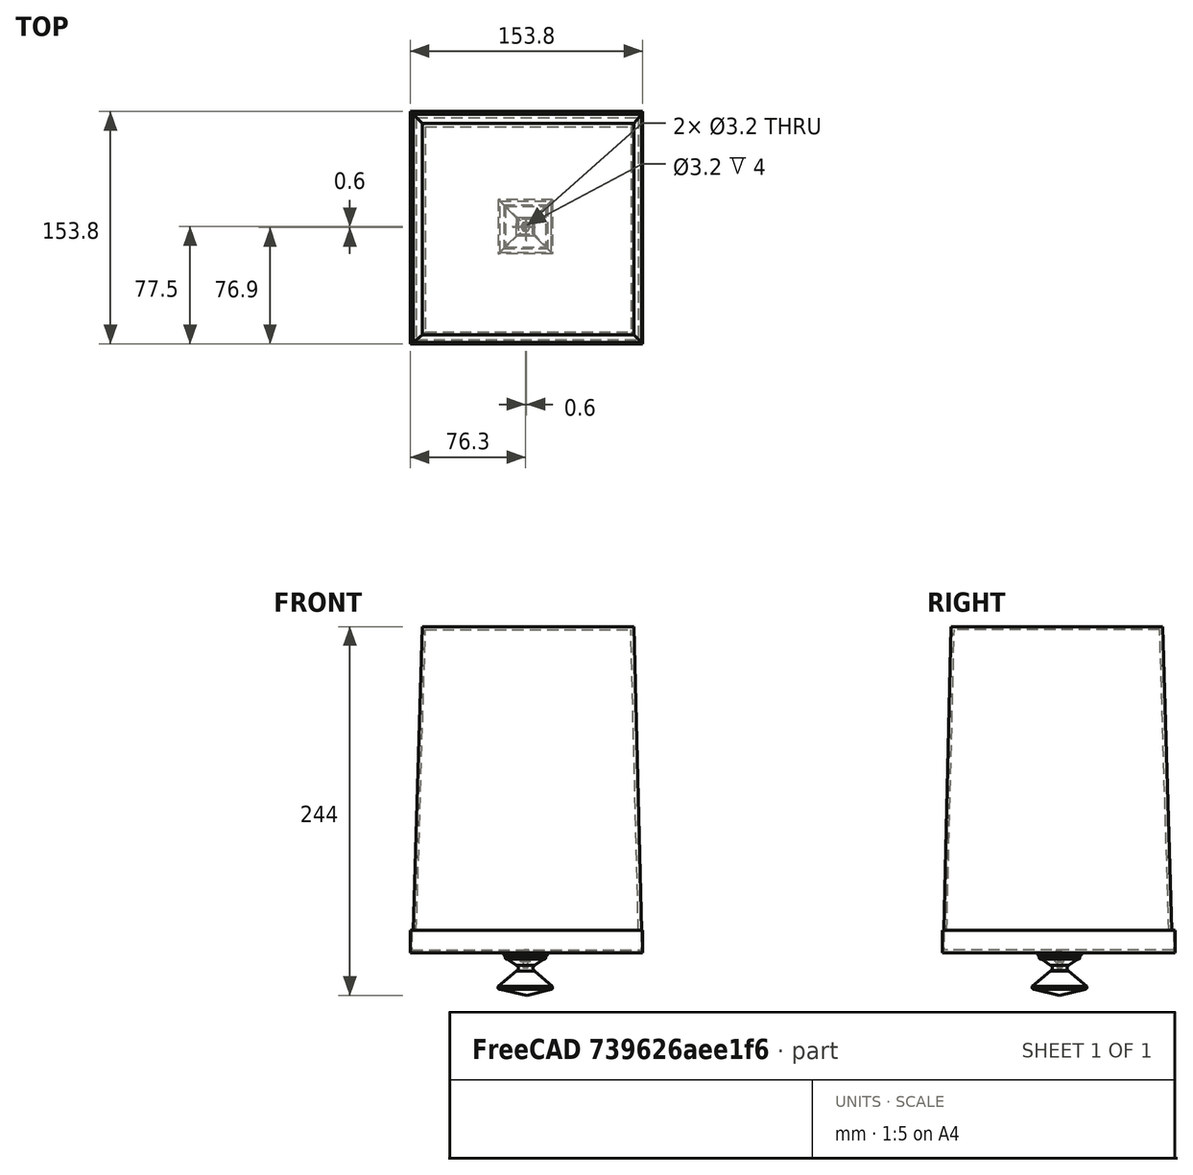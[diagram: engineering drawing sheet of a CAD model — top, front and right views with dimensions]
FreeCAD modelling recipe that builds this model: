
FCSTD DOCUMENT  (FreeCAD 0.21R33668 +26 (Git))
Label: wastebasket
License: All rights reserved
LicenseURL: http://en.wikipedia.org/wiki/All_rights_reserved
objects: PartDesign::AdditiveBox×5, PartDesign::AdditiveWedge×4, PartDesign::Fillet×4, PartDesign::Body×3, PartDesign::SubtractiveCylinder×3, PartDesign::SubtractiveWedge×1, PartDesign::SubtractiveBox×1, PartDesign::SubtractivePrism×1, PartDesign::PolarPattern×1, Mesh::Feature×1
note: 42 computed .brp shape members not serialized (recipe doc carries the construction recipe); baked Part::Feature solids carry a one-line shape summary decoded from their .brp

FEATURE [PartDesign::AdditiveWedge] Wedge  label="basket"
  AttacherType = Attacher::AttachEngine3D
  MapMode = 5
  Placement = pos=(0,0,0) rot=(1,0,0;1.5708rad)
  Support = -> [XZ_Plane]
  X2max = 146
  X2min = 6
  Xmax = 151
  Xmin = 0
  Ymax = 201
  Ymin = 0
  Z2max = 146
  Z2min = 6
  Zmax = 151
  Zmin = 0
FEATURE [PartDesign::SubtractiveWedge] Wedge001
  AttacherType = Attacher::AttachEngine3D
  BaseFeature = -> Wedge
  MapMode = 5
  Placement = pos=(0,0,0) rot=(1,0,0;1.5708rad)
  Support = -> [XZ_Plane]
  X2max = 144
  X2min = 8
  Xmax = 149
  Xmin = 2
  Ymax = 199
  Ymin = 0
  Z2max = 144
  Z2min = 8
  Zmax = 149
  Zmin = 2
  expr: X2max = <<basket>>.X2max - 2 mm
  expr: X2min = <<basket>>.X2min + 2 mm
  expr: Xmax = <<basket>>.Xmax - 2 mm
  expr: Xmin = <<basket>>.Xmin + 2 mm
  expr: Ymax = <<basket>>.Ymax - 2 mm
  expr: Z2max = <<basket>>.Z2max - 2 mm
  expr: Z2min = <<basket>>.Z2min + 2 mm
  expr: Zmax = <<basket>>.Zmax - 2 mm
  expr: Zmin = <<basket>>.Zmin + 2 mm
FEATURE [PartDesign::Body] Body
  Group = -> [Wedge,Wedge001]
  Origin = -> Origin
  Tip = -> Wedge001
FEATURE [PartDesign::AdditiveBox] Box
  AttacherType = Attacher::AttachEngine3D
  AttachmentOffset = pos=(-2,-2,0) rot=(0,0,1;0rad)
  Height = 15
  Length = 153.8
  MapMode = 5
  Placement = pos=(-2,2,0) rot=(1,0,0;3.14159rad)
  Support = -> [Wedge001]
  Width = 153.8
FEATURE [PartDesign::SubtractiveBox] Box001
  AttacherType = Attacher::AttachEngine3D
  AttachmentOffset = pos=(0.9,0.9,-15) rot=(0,0,1;0rad)
  BaseFeature = -> Box
  Height = 13
  Length = 152
  MapMode = 5
  Placement = pos=(-1.1,1.1,0) rot=(1,0,0;3.14159rad)
  Support = -> [Box]
  Width = 152
FEATURE [PartDesign::AdditiveBox] Box002
  AttacherType = Attacher::AttachEngine3D
  AttachmentOffset = pos=(61,61,0) rot=(0,0,1;0rad)
  Height = 2
  Length = 28.8
  MapMode = 5
  Placement = pos=(59.9,-59.9,-15) rot=(1,0,0;3.14159rad)
  Support = -> [Box001]
  Width = 28.8
FEATURE [PartDesign::Fillet] Fillet
  Base = -> Box002 [Face6]
  BaseFeature = -> Box002
  Placement = pos=(59.9,-59.9,-15) rot=(1,0,0;3.14159rad)
  Radius = 1
  SupportTransform = false
  UseAllEdges = false
FEATURE [PartDesign::AdditiveBox] Box003
  AttacherType = Attacher::AttachEngine3D
  AttachmentOffset = pos=(1,1,0) rot=(0,0,1;0rad)
  BaseFeature = -> Fillet
  Height = 2
  Length = 26.8
  MapMode = 5
  Placement = pos=(60.9,-60.9,-17) rot=(1,0,0;3.14159rad)
  Support = -> [Fillet]
  Width = 26.8
  expr: Length = <<Box002>>.Length - 2 mm
  expr: Width = <<Box002>>.Width - 2 mm
FEATURE [PartDesign::AdditiveWedge] Wedge002
  AttacherType = Attacher::AttachEngine3D
  AttachmentOffset = pos=(1.25,25.5,0) rot=(1,0,0;1.5708rad)
  BaseFeature = -> Box003
  MapMode = 5
  Placement = pos=(62.15,-86.4,-19) rot=(1,0,0;4.71239rad)
  Support = -> [Box003]
  X2max = 18.15
  X2min = 6.15
  Xmax = 24.3
  Xmin = 0
  Ymax = 4
  Ymin = 0
  Z2max = 18.15
  Z2min = 6.15
  Zmax = 24.3
  Zmin = 0
  expr: X2max = Xmax / 2 + 6 mm
  expr: X2min = X2max - 12 mm
  expr: Xmax = <<Box003>>.Length - 2.5 mm
  expr: Z2max = X2max
  expr: Z2min = X2min
  expr: Zmax = Xmax
FEATURE [PartDesign::Fillet] Fillet001
  Base = -> Wedge002 [Face12]
  BaseFeature = -> Wedge002
  Placement = pos=(62.15,-86.4,-19) rot=(-1,0,0;1.5708rad)
  Radius = 0.75
  SupportTransform = false
  UseAllEdges = false
FEATURE [PartDesign::Fillet] Fillet002
  Base = -> Fillet001 [Edge51,Edge55,Edge49,Edge53]
  BaseFeature = -> Fillet001
  Placement = pos=(62.15,-86.4,-19) rot=(-1,0,0;1.5708rad)
  Radius = 1
  SupportTransform = false
  UseAllEdges = false
FEATURE [PartDesign::AdditiveBox] Box004
  AttacherType = Attacher::AttachEngine3D
  AttachmentOffset = pos=(-18,6,4) rot=(0,0,1;0rad)
  BaseFeature = -> Fillet002
  Height = 4
  Length = 12
  MapMode = 5
  Placement = pos=(80.15,-80.4,-23) rot=(0,1,0;3.14159rad)
  Support = -> [Wedge002]
  Width = 12
  expr: .AttachmentOffset.Base.z = Height
FEATURE [PartDesign::AdditiveWedge] Wedge003
  AttacherType = Attacher::AttachEngine3D
  AttachmentOffset = pos=(0,12,0) rot=(1,0,0;1.5708rad)
  BaseFeature = -> Box004
  MapMode = 5
  Placement = pos=(80.15,-68.4,-27) rot=(0,0.707107,-0.707107;3.14159rad)
  Support = -> [Box004]
  X2max = 24
  X2min = -12
  Xmax = 12
  Xmin = 0
  Ymax = 10
  Ymin = 0
  Z2max = 24
  Z2min = -12
  Zmax = 12
  Zmin = 0
  expr: X2max = 30 mm - Xmax / 2
  expr: X2min = -X2max + Xmax
  expr: Z2max = X2max
  expr: Z2min = X2min
  expr: Zmax = Xmax
FEATURE [PartDesign::AdditiveBox] Box005
  AttacherType = Attacher::AttachEngine3D
  AttachmentOffset = pos=(-24,-12,0) rot=(0,0,1;0rad)
  BaseFeature = -> Wedge003
  Height = 2
  Length = 36
  MapMode = 5
  Placement = pos=(56.15,-56.4,-37) rot=(1,0,0;3.14159rad)
  Support = -> [Wedge003]
  Width = 36
  expr: Length = <<Wedge003>>.X2max - <<Wedge003>>.X2min
  expr: Width = Length
FEATURE [PartDesign::Fillet] Fillet003
  Base = -> Box005 [Face48]
  BaseFeature = -> Box005
  Placement = pos=(56.15,-56.4,-37) rot=(1,0,0;3.14159rad)
  Radius = 1
  SupportTransform = false
  UseAllEdges = false
FEATURE [PartDesign::SubtractivePrism] Prism
  AttacherType = Attacher::AttachEngine3D
  AttachmentOffset = pos=(18.15,-17.9,-6) rot=(0,0,1;0rad)
  BaseFeature = -> Fillet003
  Circumradius = 3.25
  FirstAngle = 0
  Height = 3
  MapMode = 5
  Placement = pos=(74.3,-74.3,-21) rot=(0,0,1;0rad)
  Polygon = 6
  SecondAngle = 0
  Support = -> [Fillet003]
  expr: Circumradius = 6.5 / 2
FEATURE [PartDesign::SubtractiveCylinder] Cylinder
  Angle = 360
  AttacherType = Attacher::AttachEngine3D
  AttachmentOffset = pos=(0,0,-10) rot=(0,0,1;0rad)
  BaseFeature = -> Prism
  FirstAngle = 0
  Height = 10
  MapMode = 5
  Placement = pos=(74.3,-74.3,-25) rot=(0,0,1;0rad)
  Radius = 1.6
  SecondAngle = 0
  Support = -> [Prism]
FEATURE [PartDesign::AdditiveWedge] Wedge004
  AttacherType = Attacher::AttachEngine3D
  AttachmentOffset = pos=(-5,6,0) rot=(1,0,0;1.5708rad)
  BaseFeature = -> Cylinder
  MapMode = 5
  Placement = pos=(69.3,-80.3,-39) rot=(1,0,0;4.71239rad)
  Support = -> [Cylinder]
  X2max = 6
  X2min = 6
  Xmax = 22
  Xmin = -12
  Ymax = 4
  Ymin = 0
  Z2max = 6
  Z2min = 6
  Zmax = 23
  Zmin = -11
  expr: X2min = X2max
  expr: Z2max = X2max
  expr: Z2min = X2max
FEATURE [PartDesign::SubtractiveCylinder] Cylinder001
  Angle = 360
  AttacherType = Attacher::AttachEngine3D
  AttachmentOffset = pos=(-14,12,1) rot=(1,0,0;1.5708rad)
  BaseFeature = -> Wedge004
  FirstAngle = 0
  Height = 13
  MapMode = 5
  Placement = pos=(81.15,-68.3,-25) rot=(0.57735,0.57735,-0.57735;2.0944rad)
  Radius = 2
  SecondAngle = 0
  Support = -> [Wedge004]
FEATURE [PartDesign::PolarPattern] PolarPattern
  Angle = 360
  Axis = -> Cylinder001 [Edge135]
  BaseFeature = -> Cylinder001
  Occurrences = 4
  Originals = -> [Cylinder001]
  Placement = pos=(81.15,-68.3,-25) rot=(0.57735,0.57735,-0.57735;2.0944rad)
FEATURE [PartDesign::Body] Body002
  Group = -> [Box002,Fillet,Box003,Wedge002,Fillet001,Fillet002,Box004,Wedge003,Box005,Fillet003,Prism,Cylinder,Wedge004,Cylinder001,PolarPattern]
  Origin = -> Origin002
  Tip = -> PolarPattern
FEATURE [Mesh::Feature] handle
FEATURE [PartDesign::SubtractiveCylinder] Cylinder002
  Angle = 360
  AttacherType = Attacher::AttachEngine3D
  AttachmentOffset = pos=(76,-76,-6.5) rot=(0,0,1;0rad)
  BaseFeature = -> Box001
  FirstAngle = 0
  Height = 10
  MapMode = 5
  Placement = pos=(74.9,-74.9,-19.5) rot=(0,0,1;0rad)
  Radius = 1.6
  SecondAngle = 0
  Support = -> [Box001]
  expr: .AttachmentOffset.Base.x = <<Box001>>.Width / 2
  expr: .AttachmentOffset.Base.y = -<<Box001>>.Width / 2
  expr: .AttachmentOffset.Base.z = -<<Box001>>.Height / 2
FEATURE [PartDesign::Body] Body001
  Group = -> [Box,Box001,Cylinder002]
  Origin = -> Origin001
  Tip = -> Cylinder002
